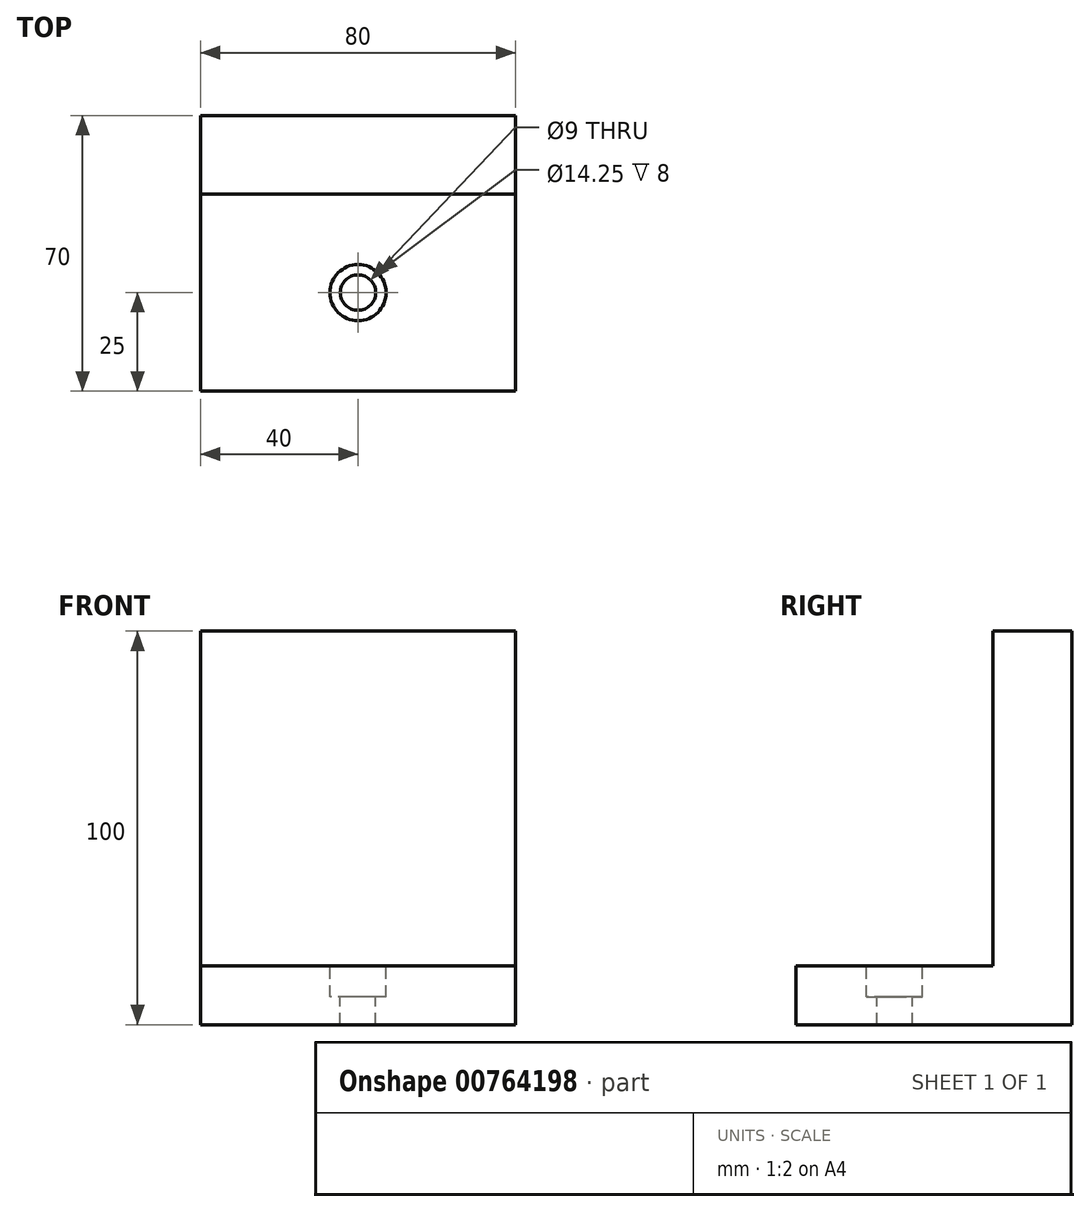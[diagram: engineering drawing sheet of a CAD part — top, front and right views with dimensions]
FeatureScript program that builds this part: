
annotation { "Feature Type Name" : "Feature", "Feature Type Description" : "" }
export const myFeature = defineFeature(function(context is Context, id is Id, definition is map)
    precondition{}
    {
        {
            var Q0;
            Q0=qCreatedBy(makeId("Right.planeOp"),FACE);
            var sketch = newSketch(context, id + "F0", { "sketchPlane" : qUnion([Q0])});
            skLineSegment(sketch, "E0", {"start": v(0, 0) * mm, "end": v(70, 0) * mm});
            skLineSegment(sketch, "E1", {"start": v(70, 0) * mm, "end": v(70, 100) * mm});
            skLineSegment(sketch, "E2", {"start": v(70, 100) * mm, "end": v(50, 100) * mm});
            skLineSegment(sketch, "E3", {"start": v(50, 100) * mm, "end": v(50, 15) * mm});
            skLineSegment(sketch, "E4", {"start": v(50, 15) * mm, "end": v(0, 15) * mm});
            skLineSegment(sketch, "E5", {"start": v(0, 15) * mm, "end": v(0, 0) * mm});
            skSolve(sketch);
        }
        {
            var Q0;
            Q0 = qSketchRegion(id + "F0", true);
            extrude(context, id + "F1", {"entities" : qUnion([Q0]), "endBound" : BoundingType.SYMMETRIC, "depth" : 80 * mm, "offsetDistance" : 25 * mm});
        }
        {
            var Q0;
            Q0=makeQuery(id+"F1.opExtrude","SWEPT_FACE",FACE,{"disambiguationData":[OSD([sQuery(id+"F0.wireOp",EDGE,"E4")])]});
            var sketch = newSketch(context, id + "F2", { "sketchPlane" : qUnion([Q0])});
            skLineSegment(sketch, "E6", {"start": v(0, 0) * mm, "end": v(0, 25) * mm});
            skSolve(sketch);
        }
        {
            var Q0;
            Q0=sQuery(id+"F2.wireOp",VERTEX,"E6.end");
            var Q1;
            Q1=makeQuery(id+"F1.opExtrude","SWEPT_BODY",BODY,{"disambiguationData":[OSD([sQuery(id+"F0.wireOp",EDGE,"E0"),sQuery(id+"F0.wireOp",EDGE,"E1"),sQuery(id+"F0.wireOp",EDGE,"E2"),sQuery(id+"F0.wireOp",EDGE,"E3"),sQuery(id+"F0.wireOp",EDGE,"E4"),sQuery(id+"F0.wireOp",EDGE,"E5")])]});
            hole(context, id + "F3", {"style" : HoleStyle.C_BORE, "endStyle" : HoleEndStyle.THROUGH, "standardTappedOrClearance" : lookupTablePath({ "fit" : "Normal", "standard" : "ISO", "size" : "M8", "type" : "Clearance" }), "standardBlindInLast" : lookupTablePath({ "fit" : "Normal", "standard" : "ISO", "engagement" : "75%", "pitch" : "1.25 mm", "size" : "M8", "type" : "Clearance & tapped" }), "holeDiameter" : 9 * mm, "cBoreDiameter" : 14.25 * mm, "cBoreDepth" : 8 * mm, "majorDiameter" : 5 * mm, "isTappedThrough" : true, "tappedDepth" : 12 * mm, "tapClearance" : 3, "locations" : qUnion([Q0]), "scope" : qUnion([Q1])});
        }
    });
